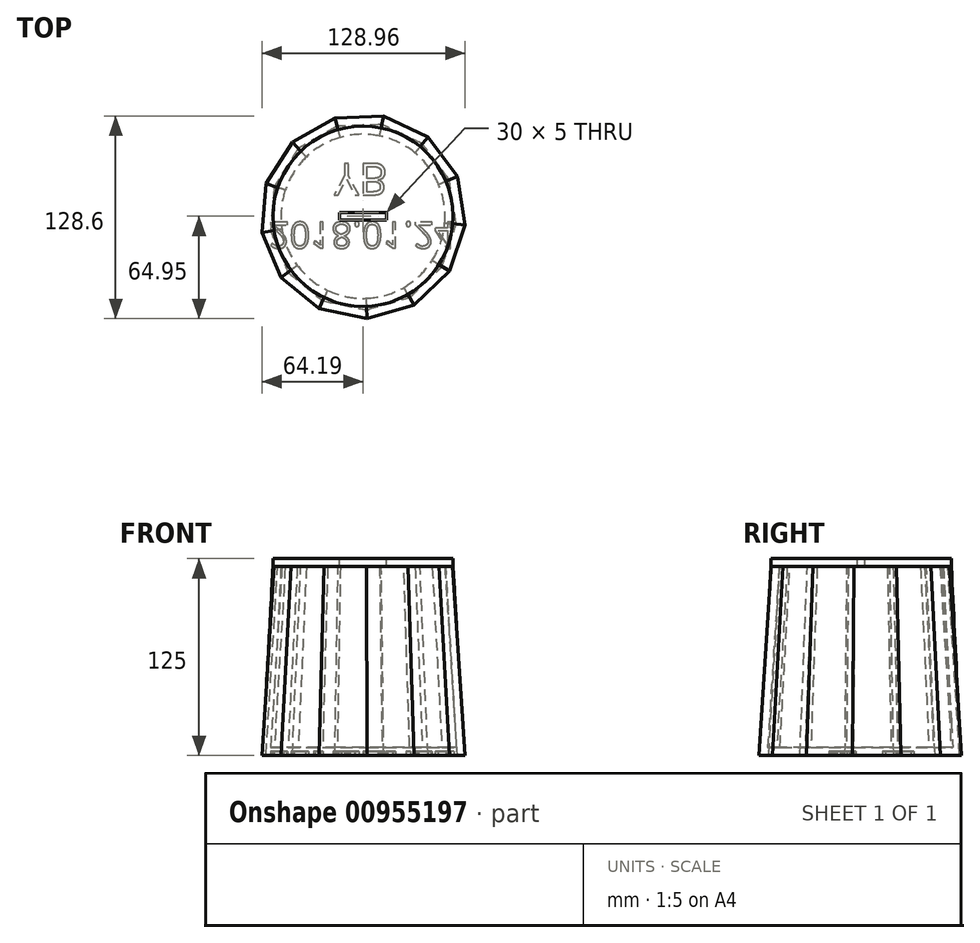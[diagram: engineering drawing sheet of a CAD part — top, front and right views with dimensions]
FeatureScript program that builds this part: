
annotation { "Feature Type Name" : "Feature", "Feature Type Description" : "" }
export const myFeature = defineFeature(function(context is Context, id is Id, definition is map)
    precondition{}
    {
        {
            var Q0;
            Q0=qCreatedBy(makeId("Top.planeOp"),FACE);
            var sketch = newSketch(context, id + "F0", { "sketchPlane" : qUnion([Q0])});
            skCircle(sketch, "E0.cCircle", {"center": v(0, 0) * mm, "radius": 65 * mm, "construction": true});
            skLineSegment(sketch, "E0.0", {"start": v(32.34, -56.39) * mm, "end": v(2.43, -64.95) * mm});
            skLineSegment(sketch, "E0.1", {"start": v(2.43, -64.95) * mm, "end": v(-28.03, -58.64) * mm});
            skLineSegment(sketch, "E0.2", {"start": v(-28.03, -58.64) * mm, "end": v(-52.08, -38.9) * mm});
            skLineSegment(sketch, "E0.3", {"start": v(-52.08, -38.9) * mm, "end": v(-64.19, -10.24) * mm});
            skLineSegment(sketch, "E0.4", {"start": v(-64.19, -10.24) * mm, "end": v(-61.6, 20.76) * mm});
            skLineSegment(sketch, "E0.5", {"start": v(-61.6, 20.76) * mm, "end": v(-44.9, 47) * mm});
            skLineSegment(sketch, "E0.6", {"start": v(-44.9, 47) * mm, "end": v(-17.9, 62.49) * mm});
            skLineSegment(sketch, "E0.7", {"start": v(-17.9, 62.49) * mm, "end": v(13.19, 63.65) * mm});
            skLineSegment(sketch, "E0.8", {"start": v(13.19, 63.65) * mm, "end": v(41.25, 50.23) * mm});
            skLineSegment(sketch, "E0.9", {"start": v(41.25, 50.23) * mm, "end": v(59.87, 25.3) * mm});
            skLineSegment(sketch, "E0.10", {"start": v(59.87, 25.3) * mm, "end": v(64.77, -5.42) * mm});
            skLineSegment(sketch, "E0.11", {"start": v(64.77, -5.42) * mm, "end": v(54.84, -34.9) * mm});
            skLineSegment(sketch, "E0.12", {"start": v(54.84, -34.9) * mm, "end": v(32.34, -56.39) * mm});
            skSolve(sketch);
        }
        {
            var Q0;
            Q0=qCreatedBy(makeId("Top.planeOp"),FACE);
            cPlane(context, id + "F1", {"entities" : qUnion([Q0]), "cplaneType" : CPlaneType.OFFSET, "offset" : 120 * mm, "width" : 152.4 * mm, "height" : 152.4 * mm});
        }
        {
            var Q0;
            Q0=qCreatedBy(id+"F1.planeOp",FACE);
            var sketch = newSketch(context, id + "F2", { "sketchPlane" : qUnion([Q0])});
            skCircle(sketch, "E1", {"center": v(0, 0) * mm, "radius": 57.2 * mm});
            skSolve(sketch);
        }
        {
            var Q0;
            Q0=makeQuery(id+"F0.imprint","IMPRINT",FACE,{"disambiguationData":[TD([[makeQuery(id+"F0.imprint","IMPRINT",EDGE,{"derivedFrom":sQuery(id+"F0.wireOp",EDGE,"E0.0")}),-1.0]])]});
            var Q1;
            Q1=makeQuery(id+"F2.imprint","IMPRINT",FACE,{"disambiguationData":[TD([[makeQuery(id+"F2.imprint","IMPRINT",EDGE,{"derivedFrom":sQuery(id+"F2.wireOp",EDGE,"E1")}),1.0]])]});
            loft(context, id + "F3", {"sheetProfilesArray" : [{ "sheetProfileEntities" : qUnion([Q0]) }, { "sheetProfileEntities" : qUnion([Q1]) }]});
        }
        {
            var Q0;
            Q0=makeQuery(id+"F3.opLoft","CAP_FACE",FACE,{"disambiguationData":[OSD([makeQuery(id+"F2.imprint","IMPRINT",FACE,{"disambiguationData":[TD([[makeQuery(id+"F2.imprint","IMPRINT",EDGE,{"derivedFrom":sQuery(id+"F2.wireOp",EDGE,"E1")}),1.0]])]})])],"isStart":true});
            shell(context, id + "F4", {"entities" : qUnion([Q0]), "thickness" : 5.08 * mm});
        }
        {
            var Q0;
            Q0=qCreatedBy(id+"F1.planeOp",FACE);
            var sketch = newSketch(context, id + "F5", { "sketchPlane" : qUnion([Q0])});
            skCircle(sketch, "E2", {"center": v(0, 0) * mm, "radius": 57.2 * mm});
            skSolve(sketch);
        }
        {
            var Q0;
            Q0 = qSketchRegion(id + "F5", true);
            extrude(context, id + "F6", {"entities" : qUnion([Q0]), "depth" : 5 * mm, "offsetDistance" : 25.4 * mm});
        }
        {
            var Q0;
            Q0=makeQuery(id+"F6.opExtrude","CAP_FACE",FACE,{"disambiguationData":[OSD([sQuery(id+"F5.wireOp",EDGE,"E2")])],"isStart":false});
            var sketch = newSketch(context, id + "F7", { "sketchPlane" : qUnion([Q0])});
            skLineSegment(sketch, "E3.bottom", {"start": v(-15, 2.5) * mm, "end": v(15, 2.5) * mm});
            skLineSegment(sketch, "E3.top", {"start": v(-15, -2.5) * mm, "end": v(15, -2.5) * mm});
            skLineSegment(sketch, "E3.left", {"start": v(-15, 2.5) * mm, "end": v(-15, -2.5) * mm});
            skLineSegment(sketch, "E3.right", {"start": v(15, 2.5) * mm, "end": v(15, -2.5) * mm});
            skPoint(sketch, "E3.middle", {"position": v(0, 0) * mm});
            skSolve(sketch);
        }
        {
            var Q0;
            Q0=makeQuery(id+"F7.imprint","IMPRINT",FACE,{"disambiguationData":[TD([[makeQuery(id+"F7.imprint","IMPRINT",EDGE,{"derivedFrom":sQuery(id+"F7.wireOp",EDGE,"E3.bottom")}),-1.0]])]});
            extrude(context, id + "F8", {"entities" : qUnion([Q0]), "operationType" : NewBodyOperationType.REMOVE, "oppositeDirection" : true, "depth" : 25.4 * mm, "offsetDistance" : 25.4 * mm});
        }
        {
            var Q0;
            {var subQ4=sQuery(id+"F0.wireOp",EDGE,"E0.0");Q0=makeQuery(id+"FUe3jObyvxc5PrZ_2.boolean.opBoolean","SPLIT",FACE,{"disambiguationData":[TD([makeQuery(id+"FUe3jObyvxc5PrZ_2.opExtrude","SWEPT_FACE",FACE,{"disambiguationData":[OSD([sQuery(id+"F7wMkUPvId49nod_2.wireOp",EDGE,"5999bbf5-4f7d-4c48-9bb3-27212876aee2.sketch_text.stroke-0")])]})])],"derivedFrom":makeQuery(id+"F3.opLoft","CAP_FACE",FACE,{"disambiguationData":[OSD([makeQuery(id+"F0.imprint","IMPRINT",FACE,{"disambiguationData":[TD([[makeQuery(id+"F0.imprint","IMPRINT",EDGE,{"derivedFrom":subQ4}),-1.0]])]})])],"isStart":true})});}
            var sketch = newSketch(context, id + "F9", { "sketchPlane" : qUnion([Q0])});
            skText(sketch, "E4", { "text": "2018.01.24", "fontName": "OpenSans-Regular.ttf"});
            const initialGuessF9  = {"E4": [-0.05996, 0.00369, 1, 0, 0.01669]};
            skSetInitialGuess(sketch, initialGuessF9);
            skSolve(sketch);
        }
        {
            var Q0;
            Q0=makeQuery(id+"F9.imprint","IMPRINT",FACE,{"disambiguationData":[TD([[makeQuery(id+"F9.imprint","IMPRINT",EDGE,{"derivedFrom":sQuery(id+"F9.wireOp",EDGE,"E4.sketch_text.stroke-0")}),1.0]])]});
            var sketch = newSketch(context, id + "F10", { "sketchPlane" : qUnion([Q0])});
            skText(sketch, "E5", { "text": "YB", "fontName": "OpenSans-Regular.ttf"});
            const initialGuessF10  = {"E5": [-0.01837, -0.03357, 1, 0, 0.02023]};
            skSetInitialGuess(sketch, initialGuessF10);
            skSolve(sketch);
        }
        {
            var Q0;
            Q0 = qSketchRegion(id + "F10", true);
            var Q1;
            Q1 = qSketchRegion(id + "F9", true);
            extrude(context, id + "F11", {"entities" : qUnion([Q0, Q1]), "operationType" : NewBodyOperationType.REMOVE, "oppositeDirection" : true, "depth" : 2.54 * mm, "offsetDistance" : 25.4 * mm});
        }
    });
